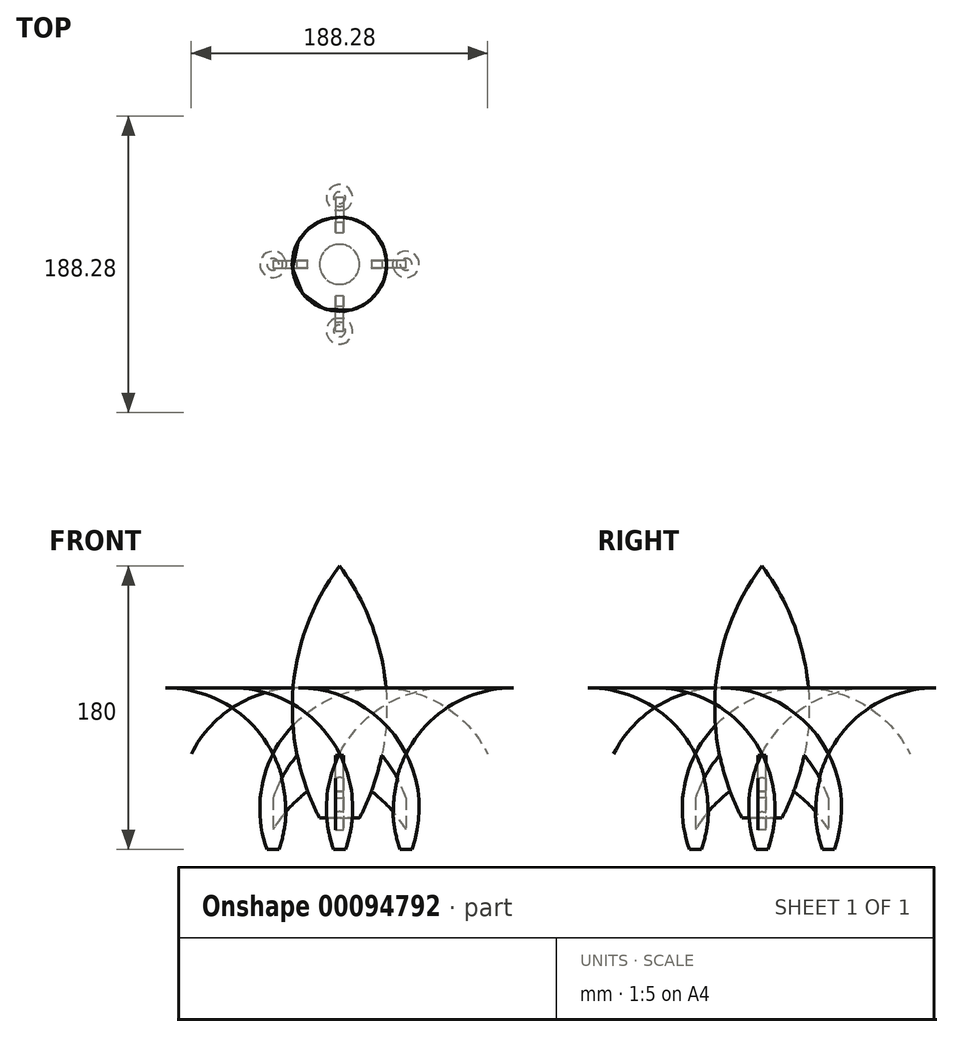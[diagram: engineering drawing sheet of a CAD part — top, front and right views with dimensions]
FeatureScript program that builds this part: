
annotation { "Feature Type Name" : "Feature", "Feature Type Description" : "" }
export const myFeature = defineFeature(function(context is Context, id is Id, definition is map)
    precondition{}
    {
        {
            var Q0;
            Q0=qCreatedBy(makeId("Front.planeOp"),FACE);
            var sketch = newSketch(context, id + "F0", { "sketchPlane" : qUnion([Q0])});
            skArc(sketch, "E0", {"start": v(12.66, 20) * mm, "mid": v(29.53, 101.84) * mm, "end": v(0, 180) * mm});
            skLineSegment(sketch, "E1", {"start": v(12.66, 20) * mm, "end": v(0, 20) * mm});
            skLineSegment(sketch, "E2", {"start": v(0, 20) * mm, "end": v(0, 180) * mm});
            skPoint(sketch, "E3.orphan", {"position": v(0, 0) * mm});
            skLineSegment(sketch, "E4", {"start": v(0, 213.92) * mm, "end": v(0, -16.52) * mm, "construction": true});
            skSolve(sketch);
        }
        {
            var Q0;
            Q0=makeQuery(id+"F0.imprint","IMPRINT",FACE,{"disambiguationData":[TD([[makeQuery(id+"F0.imprint","IMPRINT",EDGE,{"derivedFrom":sQuery(id+"F0.wireOp",EDGE,"E0")}),1.0]])]});
            var Q1;
            Q1=sQuery(id+"F0.wireOp",EDGE,"E4");
            revolve(context, id + "F1", {"entities" : qUnion([Q0]), "axis" : qUnion([Q1]), "revolveType" : RevolveType.FULL});
        }
        {
            var Q0;
            Q0=qCreatedBy(makeId("Front.planeOp"),FACE);
            var sketch = newSketch(context, id + "F2", { "sketchPlane" : qUnion([Q0])});
            skArc(sketch, "E5", {"start": v(42.28, 32.66) * mm, "mid": v(25.8, 61.06) * mm, "end": v(0, 81.39) * mm});
            skArc(sketch, "E6", {"start": v(42.28, 12.54) * mm, "mid": v(24.08, 33.79) * mm, "end": v(0, 48.04) * mm});
            skLineSegment(sketch, "E7", {"start": v(42.28, 32.66) * mm, "end": v(42.28, 12.54) * mm});
            skLineSegment(sketch, "E8", {"start": v(0, 48.04) * mm, "end": v(0, 81.39) * mm});
            skSolve(sketch);
        }
        {
            var Q0;
            Q0=makeQuery(id+"F2.imprint","IMPRINT",FACE,{"disambiguationData":[TD([[makeQuery(id+"F2.imprint","IMPRINT",EDGE,{"derivedFrom":sQuery(id+"F2.wireOp",EDGE,"E5")}),1.0]])]});
            extrude(context, id + "F3", {"entities" : qUnion([Q0]), "operationType" : NewBodyOperationType.ADD, "endBound" : BoundingType.SYMMETRIC, "depth" : 5 * mm});
        }
        {
            var Q0;
            Q0=qCreatedBy(makeId("Front.planeOp"),FACE);
            var sketch = newSketch(context, id + "F4", { "sketchPlane" : qUnion([Q0])});
            skLineSegment(sketch, "E9", {"start": v(0, 196.6) * mm, "end": v(0, -75.83) * mm, "construction": true});
            skSolve(sketch);
        }
        {
            var Q0;
            Q0=makeQuery(id+"F1.opRevolve","SWEPT_BODY",BODY,{"disambiguationData":[OSD([sQuery(id+"F0.wireOp",EDGE,"E0"),sQuery(id+"F0.wireOp",EDGE,"E1"),sQuery(id+"F0.wireOp",EDGE,"E2")])]});
            var Q1;
            Q1=sQuery(id+"F4.wireOp",EDGE,"E9");
            circularPattern(context, id + "F5", {"operationType" : NewBodyOperationType.ADD, "entities" : qUnion([Q0]), "axis" : qUnion([Q1]), "angle" : 90 * degree, "instanceCount" : 4});
        }
        {
            var Q0;
            Q0=qCreatedBy(makeId("Front.planeOp"),FACE);
            var sketch = newSketch(context, id + "F6", { "sketchPlane" : qUnion([Q0])});
            skLineSegment(sketch, "E10", {"start": v(42.28, 3.14) * mm, "end": v(42.28, 118.45) * mm, "construction": true});
            skLineSegment(sketch, "E11", {"start": v(42.28, 60.8) * mm, "end": v(42.28, 0) * mm});
            skLineSegment(sketch, "E12", {"start": v(42.28, 0) * mm, "end": v(46.04, 0) * mm});
            skArc(sketch, "E13", {"start": v(46.04, 0) * mm, "mid": v(50.47, 30.79) * mm, "end": v(42.28, 60.8) * mm});
            skSolve(sketch);
        }
        {
            var Q0;
            Q0=makeQuery(id+"F6.imprint","IMPRINT",FACE,{"disambiguationData":[TD([[makeQuery(id+"F6.imprint","IMPRINT",EDGE,{"derivedFrom":sQuery(id+"F6.wireOp",EDGE,"E11")}),1.0]])]});
            var Q1;
            Q1=sQuery(id+"F6.wireOp",EDGE,"E10");
            revolve(context, id + "F7", {"operationType" : NewBodyOperationType.ADD, "entities" : qUnion([Q0]), "axis" : qUnion([Q1]), "revolveType" : RevolveType.FULL});
        }
        {
            var Q0;
            Q0=makeQuery(id+"F1.opRevolve","SWEPT_BODY",BODY,{"disambiguationData":[OSD([sQuery(id+"F0.wireOp",EDGE,"E0"),sQuery(id+"F0.wireOp",EDGE,"E1"),sQuery(id+"F0.wireOp",EDGE,"E2")])]});
            var Q1;
            Q1=sQuery(id+"F4.wireOp",EDGE,"E9");
            circularPattern(context, id + "F8", {"entities" : qUnion([Q0]), "axis" : qUnion([Q1]), "angle" : 90 * degree, "instanceCount" : 4});
        }
    });
